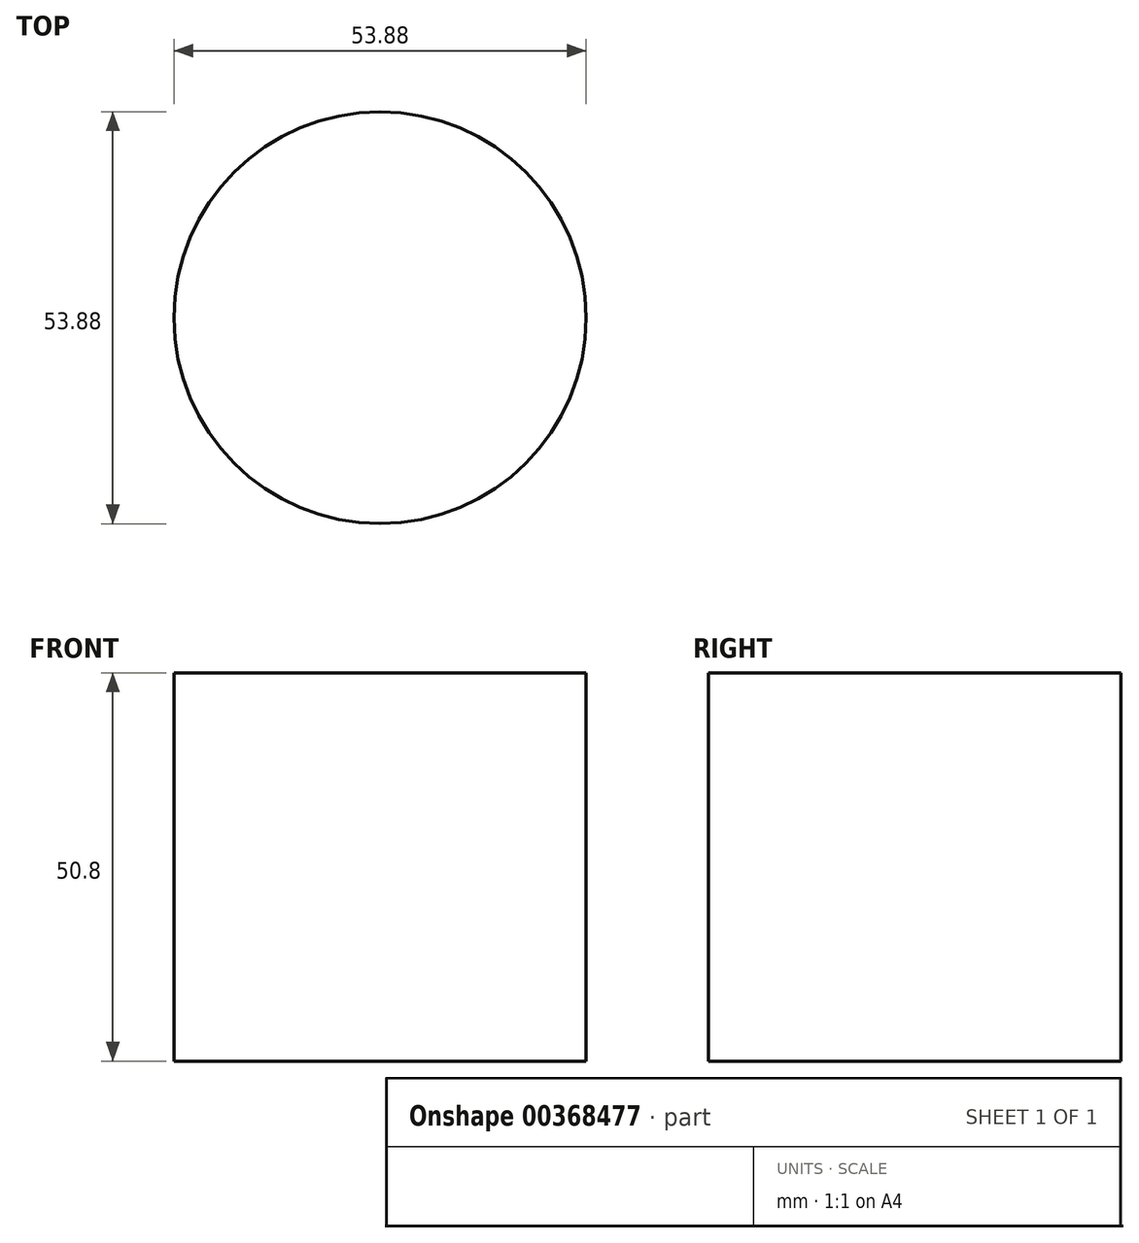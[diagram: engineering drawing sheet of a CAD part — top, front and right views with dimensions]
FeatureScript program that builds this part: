
annotation { "Feature Type Name" : "Feature", "Feature Type Description" : "" }
export const myFeature = defineFeature(function(context is Context, id is Id, definition is map)
    precondition{}
    {
        {
            var Q0;
            Q0=qCreatedBy(makeId("Top.planeOp"),FACE);
            var sketch = newSketch(context, id + "F0", { "sketchPlane" : qUnion([Q0])});
            skCircle(sketch, "E0", {"center": v(0, 0) * mm, "radius": 26.94 * mm});
            skSolve(sketch);
        }
        {
            var Q0;
            Q0=sQuery(id+"F0.wireOp",EDGE,"E0");
            extrude(context, id + "F1", {"bodyType" : ToolBodyType.SURFACE, "surfaceEntities" : qUnion([Q0]), "depth" : 50.8 * mm});
        }
    });
